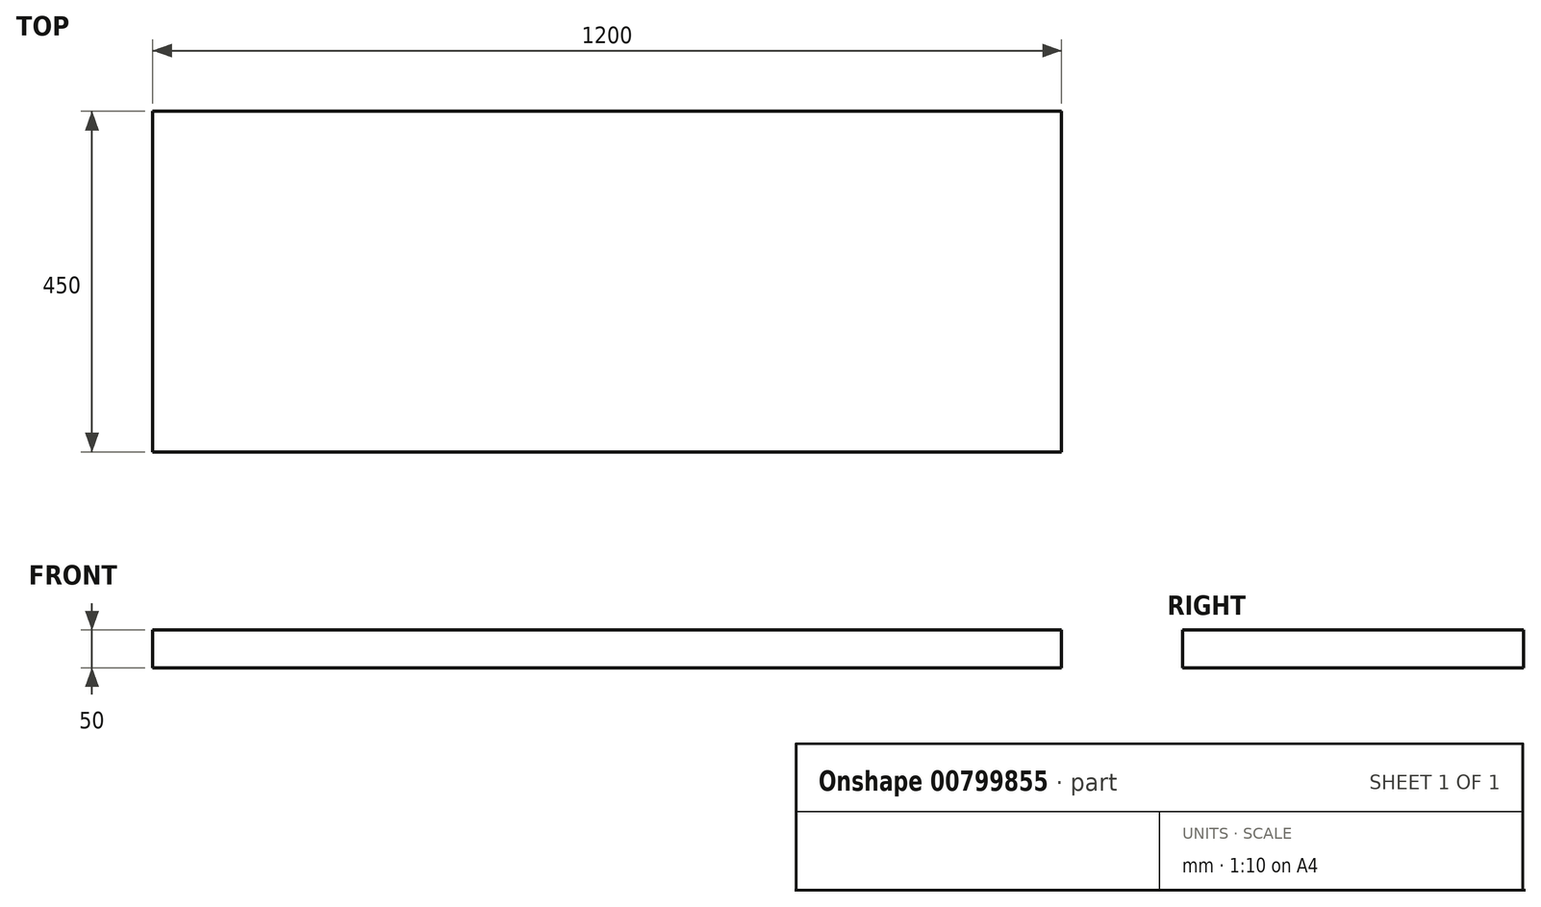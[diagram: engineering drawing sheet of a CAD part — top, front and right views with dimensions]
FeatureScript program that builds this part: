
annotation { "Feature Type Name" : "Feature", "Feature Type Description" : "" }
export const myFeature = defineFeature(function(context is Context, id is Id, definition is map)
    precondition{}
    {
        {
            var Q0;
            Q0=qCreatedBy(makeId("Top.planeOp"),FACE);
            var sketch = newSketch(context, id + "F0", { "sketchPlane" : qUnion([Q0])});
            skLineSegment(sketch, "E0", {"start": v(0, 0) * mm, "end": v(0, 0) * mm});
            skLineSegment(sketch, "E1", {"start": v(0, 0) * mm, "end": v(-400, 0) * mm});
            skLineSegment(sketch, "E2", {"start": v(-400, 0) * mm, "end": v(-400, 450) * mm});
            skLineSegment(sketch, "E3", {"start": v(-400, 450) * mm, "end": v(800, 450) * mm});
            skLineSegment(sketch, "E4", {"start": v(800, 450) * mm, "end": v(800, 0) * mm});
            skLineSegment(sketch, "E5", {"start": v(800, 0) * mm, "end": v(0, 0) * mm});
            skSolve(sketch);
        }
        {
            var Q0;
            Q0=makeQuery(id+"F0.imprint","IMPRINT",FACE,{"disambiguationData":[TD([[makeQuery(id+"F0.imprint","IMPRINT",EDGE,{"derivedFrom":sQuery(id+"F0.wireOp",EDGE,"E1")}),-1.0]])]});
            extrude(context, id + "F1", {"entities" : qUnion([Q0]), "depth" : 50 * mm, "offsetDistance" : 25 * mm});
        }
    });
